# Revit family: Lighting-Floodlights-GEWISS-ELIA-FL-L3-LED_FLOODLIGHTS
name_source: partatom
category: Apparecchi per illuminazione
units: mm (PartAtom-declared; Revit-internal decimal feet)

## family parameters
Condiviso = No
Host = Superficie
Punto di calcolo locali = Sì
Quota connettore circolare = Usa diametro
Sorgente d'illuminazione = Sì
Taglio con vuoti quando caricato = No
Tipo di parte = Normale

## types (8) — shared parameters
- = Built-in
-- = Built-in
--- = Built-in
---- = Built-in
----- = Built-in
Angolo campo riflettore = 90.00°
Angolo inclinazione = 90.00°
Angolo raggio riflettore = 90.00°
Application = Indoor / Outdoor
Body = Die-cast aluminium -
Category: = Outdoor areas
Classification: = -
Color Rendering Index = CRI 80
Colour = Black
Colour : = Powder coating
Cornice = cornice
DIN 18032-3 certification = -
Device with reduced surface temperature = -
Driver = Built-in
Driver Box = Built-in
Efficiency (lm/W): = Above 120 lm/W
Electrocod = 2424
Eletrical and lighting features = -
Emetti da lunghezza linea = 150 mm
External screw = Stainless steel
FORO_CONTROSOFFITTO = 47 mm
Filtro dei colori = 16777215
Gasket = -
General information = -
Glow Wire Test : = 750 °C
Group: = xyz
IDF = b9a8b203-7566-4ac4-964b-246ea0f0f5a1
IP degree = IP66
IPEA = -
Immagine tipo = <Nessuno>
Installationa and maintenance = -
Insulation class = I
LED = led
LED Maintenance = By professional
Larghezza_Lampada = 600 mm
Locking Hook = -
Lumen output  (lm) = Up to 25,000 lm
Luminaire = LED luminaire with mid and high lumen power
Lunghezza simbolo sorgente d'illuminazione = 3048 mm  [stored 10 ft]
Lunghezza_lampada = 600 mm
Materials = -
Maximum surface exposed to the wind : = 0,07 m²
Operating temperature : = -30°C ÷ +50 °C
Optic Maintenance = Non-replaceable
Optic and illuminating features = -
PLACCAGGIO = <Per categoria>
POSIZIONE = 80000
Photobiological Risk Class = RG1
Produttore = GEWISS S.p.A.
Prospetto di default = 1219 mm
Rated frequency (Hz) = 50/60 Hz
SEO = Floodlight
STRUTTURA = Struttura
Shock resistance = IK08
Spessore lampada = 27 mm
Standard Deviation Colour Matching = SDCM = 5
Standard- = EN 60598-1; EN 60598-2-5; IEC/TR 62778; EN 62493
Standards and approvals = -
Supply voltage = 220-240 VÂ
System  power = From 100 to 200 W
Tilt- = Rotation on bracket with integrated goniometer
Type of light source = LED
Typology: = Small systems
URL = https://www.gewiss.com
Unified Glare Rating = ULOR = 0%
Unique digital code (Datamatrix) = Currently not present
Variazione temperatura colore lampada con luminosità attenuata = <Nessuno>
Version file RFA = 20.0
Warranty = 5 years
Wiring = With power cable
ottica = Default Form

## per-type parameters (varying)
| type | Control System | Descrizione | Modello | Optic | Overvoltage protection | Stocking temperature |
| GWF1100RH857 - ELIA FL L3 150W 5700K CRI80 On/Off 60° | ON / OFF | ELIA FL L3 150W 5700K CRI80 On/Off 60° | GWF1100RH857 | 60° |  | -40° +80° |
| GWF1100RH840 - ELIA FL L3 150W 4000K CRI80 On/Off 60° | ON / OFF | ELIA FL L3 150W 4000K CRI80 On/Off 60° | GWF1100RH840 | 60° |  | -40° +80° |
| GWF1100RH830 - ELIA FL L3 150W 3000K CRI80 On/Off 60° | ON / OFF | ELIA FL L3 150W 3000K CRI80 On/Off 60° | GWF1100RH830 | 60° |  | -40° +80° |
| GWF1100RC857 - ELIA FL L3 150W 5700K CRI80 On/Off As. | ON / OFF | ELIA FL L3 150W 5700K CRI80 On/Off As. | GWF1100RC857 | Asymmetrical |  | -40° +80° |
| GWF1101RH840 - ELIA FL L3 150W 4000K CRI80 DALI 60° | DALI | ELIA FL L3 150W 4000K CRI80 DALI 60° | GWF1101RH840 | 60° | DM 6 kV / CM 10 kV |  |
| GWF1101RC840 - ELIA FL L3 150W 4000K CRI80 DALI As. | DALI | ELIA FL L3 150W 4000K CRI80 DALI As. | GWF1101RC840 | Asymmetrical | DM 6 kV / CM 10 kV |  |
| GWF1100RC830 - ELIA FL L3 150W 3000K CRI80 On/Off As. | ON / OFF | ELIA FL L3 150W 3000K CRI80 On/Off As. | GWF1100RC830 | Asymmetrical |  | -40° +80° |
| GWF1100RC840 - ELIA FL L3 150W 4000K CRI80 On/Off As. | ON / OFF | ELIA FL L3 150W 4000K CRI80 On/Off As. | GWF1100RC840 | Asymmetrical |  | -40° +80° |

note: [stored X ft] marks values corroborated as IEEE doubles in the binary element streams (Revit-internal decimal feet)

## geometry (parser evidence)
native form markers: Sweep x3
no freeform markers — native parametric forms only
